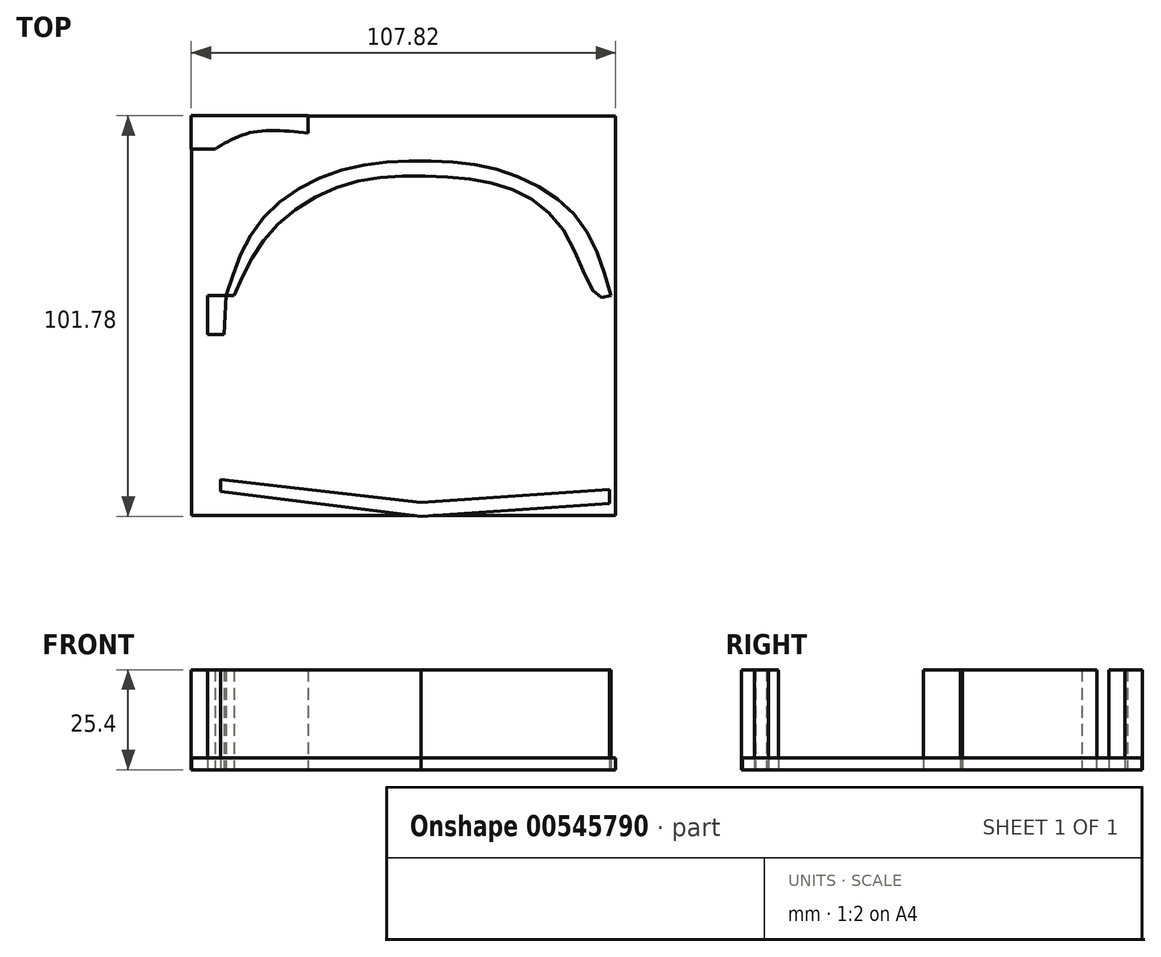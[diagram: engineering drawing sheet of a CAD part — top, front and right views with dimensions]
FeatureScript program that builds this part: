
annotation { "Feature Type Name" : "Feature", "Feature Type Description" : "" }
export const myFeature = defineFeature(function(context is Context, id is Id, definition is map)
    precondition{}
    {
        {
            var Q0;
            Q0=qCreatedBy(makeId("Top.planeOp"),FACE);
            var sketch = newSketch(context, id + "F0", { "sketchPlane" : qUnion([Q0])});
            skLineSegment(sketch, "E0", {"start": v(-49.66, 0) * mm, "end": v(-52.36, 0) * mm});
            skLineSegment(sketch, "E1", {"start": v(-52.36, 0) * mm, "end": v(-52.36, -9.96) * mm});
            skLineSegment(sketch, "E2", {"start": v(-52.36, -9.96) * mm, "end": v(-49.85, -9.96) * mm});
            skLineSegment(sketch, "E3", {"start": v(-52.36, 0) * mm, "end": v(-52.36, 37.25) * mm});
            skLineSegment(sketch, "E4", {"start": v(-52.36, 37.25) * mm, "end": v(-58.36, 37.25) * mm});
            skLineSegment(sketch, "E5", {"start": v(-58.36, 37.25) * mm, "end": v(-58.36, 45.7) * mm});
            skLineSegment(sketch, "E6", {"start": v(-58.36, 45.7) * mm, "end": v(-28.63, 45.7) * mm});
            skLineSegment(sketch, "E7", {"start": v(-28.63, 45.7) * mm, "end": v(-28.63, 41.29) * mm});
            skPoint(sketch, "E8.1.internal.snap0", {"position": v(-58.36, 41.47) * mm});
            skFitSpline(sketch, "E8", {"points": [v(-52.36, 37.25) * mm, v(-42.94, 41.47) * mm, v(-28.63, 41.29) * mm], "startDerivative": vector(19.15, 11.38) * mm, "endDerivative": vector(28.08, -2.92) * mm});
            skSolve(sketch);
        }
        {
            var Q0;
            Q0=qCreatedBy(makeId("Top.planeOp"),FACE);
            var sketch = newSketch(context, id + "F1", { "sketchPlane" : qUnion([Q0])});
            skFitSpline(sketch, "E9", {"points": [v(-49.47, 0) * mm, v(-41.08, 18.53) * mm, v(-22.12, 31.3) * mm, v(0, 34.2) * mm, v(20.56, 31.66) * mm, v(39.52, 19.98) * mm, v(48.28, 0) * mm], "startDerivative": vector(38.15, 121.72) * mm, "endDerivative": vector(37.28, -129.59) * mm});
            skLineSegment(sketch, "E10", {"start": v(-50.93, -46.76) * mm, "end": v(0, -52.6) * mm});
            skLineSegment(sketch, "E11", {"start": v(0, -52.6) * mm, "end": v(47.91, -49.31) * mm});
            skFitSpline(sketch, "E12", {"points": [v(-47.42, 0) * mm, v(-38.47, 15.81) * mm, v(-20.5, 27.8) * mm, v(0, 30.32) * mm, v(20.56, 27.8) * mm, v(36.28, 16.45) * mm, v(44.8, 0) * mm, v(48.28, 0) * mm], "startDerivative": vector(48.2, 110.72) * mm, "endDerivative": vector(54.5, 19.15) * mm});
            skFitSpline(sketch, "E13", {"points": [v(-49.47, 0) * mm, v(-47.42, 0) * mm], "startDerivative": vector(2.05, 0) * mm, "endDerivative": vector(2.05, 0) * mm});
            skLineSegment(sketch, "E14", {"start": v(-50.93, -46.76) * mm, "end": v(-50.93, -49.78) * mm});
            skLineSegment(sketch, "E15", {"start": v(-50.93, -49.78) * mm, "end": v(0, -56.1) * mm});
            skLineSegment(sketch, "E16", {"start": v(0, -56.1) * mm, "end": v(47.87, -52.81) * mm});
            skLineSegment(sketch, "E17", {"start": v(47.87, -52.81) * mm, "end": v(47.91, -49.31) * mm});
            skSolve(sketch);
        }
        {
            var Q0;
            Q0=makeQuery(id+"F1.imprint","IMPRINT",FACE,{"disambiguationData":[TD([[makeQuery(id+"F1.imprint","IMPRINT",EDGE,{"derivedFrom":sQuery(id+"F1.wireOp",EDGE,"E10")}),-1.0]])]});
            var Q1;
            Q1=makeQuery(id+"F1.imprint","IMPRINT",FACE,{"disambiguationData":[TD([[makeQuery(id+"F1.imprint","IMPRINT",EDGE,{"derivedFrom":sQuery(id+"F1.wireOp",EDGE,"E9")}),-1.0]])]});
            extrude(context, id + "F2", {"entities" : qUnion([Q0, Q1]), "depth" : 25.4 * mm, "offsetDistance" : 25.4 * mm});
        }
        {
            var Q0;
            Q0=qCreatedBy(makeId("Top.planeOp"),FACE);
            var sketch = newSketch(context, id + "F3", { "sketchPlane" : qUnion([Q0])});
            skLineSegment(sketch, "E18", {"start": v(-54.36, 37.27) * mm, "end": v(-52.46, 37.27) * mm});
            skSolve(sketch);
        }
        {
            var Q0;
            Q0 = qSketchRegion(id + "F3", true);
            var Q1;
            Q1=makeQuery(id+"F0.imprint","IMPRINT",FACE,{"disambiguationData":[TD([[makeQuery(id+"F0.imprint","IMPRINT",EDGE,{"derivedFrom":sQuery(id+"F0.wireOp",EDGE,"E4")}),-1.0]])]});
            extrude(context, id + "F4", {"entities" : qUnion([Q0, Q1]), "depth" : 25.4 * mm, "offsetDistance" : 25.4 * mm});
        }
        {
            var Q0;
            Q0=qCreatedBy(makeId("Top.planeOp"),FACE);
            var sketch = newSketch(context, id + "F5", { "sketchPlane" : qUnion([Q0])});
            skLineSegment(sketch, "E19", {"start": v(-52.44, 37.3) * mm, "end": v(-52.44, -9.27) * mm});
            skLineSegment(sketch, "E20", {"start": v(-52.44, -9.27) * mm, "end": v(-52.44, -9.84) * mm});
            skLineSegment(sketch, "E21", {"start": v(-52.44, -9.84) * mm, "end": v(-54.27, -9.84) * mm});
            skLineSegment(sketch, "E22", {"start": v(-54.27, -9.84) * mm, "end": v(-49.99, -9.84) * mm});
            skLineSegment(sketch, "E23", {"start": v(-49.99, -9.84) * mm, "end": v(-49.53, 0) * mm});
            skLineSegment(sketch, "E24", {"start": v(-49.53, 0) * mm, "end": v(-54.27, 0) * mm});
            skLineSegment(sketch, "E25", {"start": v(-54.27, 0) * mm, "end": v(-54.27, -9.84) * mm});
            skSolve(sketch);
        }
        {
            var Q0;
            {var subQ2=sQuery(id+"F5.wireOp",EDGE,"E20");Q0=makeQuery(id+"F5.imprint","IMPRINT",FACE,{"disambiguationData":[TD([[makeQuery(id+"F5.imprint","IMPRINT",EDGE,{"derivedFrom":subQ2}),1.0]])]});}
            var Q1;
            {var subQ1=sQuery(id+"F5.wireOp",EDGE,"E20");Q1=makeQuery(id+"F5.imprint","IMPRINT",FACE,{"disambiguationData":[TD([[makeQuery(id+"F5.imprint","IMPRINT",EDGE,{"derivedFrom":subQ1}),-1.0]])]});}
            extrude(context, id + "F6", {"entities" : qUnion([Q0, Q1]), "operationType" : NewBodyOperationType.ADD, "depth" : 25.4 * mm, "offsetDistance" : 25.4 * mm});
        }
        {
            var Q0;
            Q0=qCreatedBy(makeId("Top.planeOp"),FACE);
            var sketch = newSketch(context, id + "F7", { "sketchPlane" : qUnion([Q0])});
            skLineSegment(sketch, "E26.bottom", {"start": v(-58.27, 45.56) * mm, "end": v(49.46, 45.56) * mm});
            skLineSegment(sketch, "E26.top", {"start": v(-58.27, -55.88) * mm, "end": v(49.46, -55.88) * mm});
            skLineSegment(sketch, "E26.left", {"start": v(-58.27, 45.56) * mm, "end": v(-58.27, -55.88) * mm});
            skLineSegment(sketch, "E26.right", {"start": v(49.46, 45.56) * mm, "end": v(49.46, -55.88) * mm});
            skSolve(sketch);
        }
        {
            var Q0;
            Q0 = qSketchRegion(id + "F7", true);
            extrude(context, id + "F8", {"entities" : qUnion([Q0]), "depth" : 3 * mm, "offsetDistance" : 25 * mm});
        }
    });
